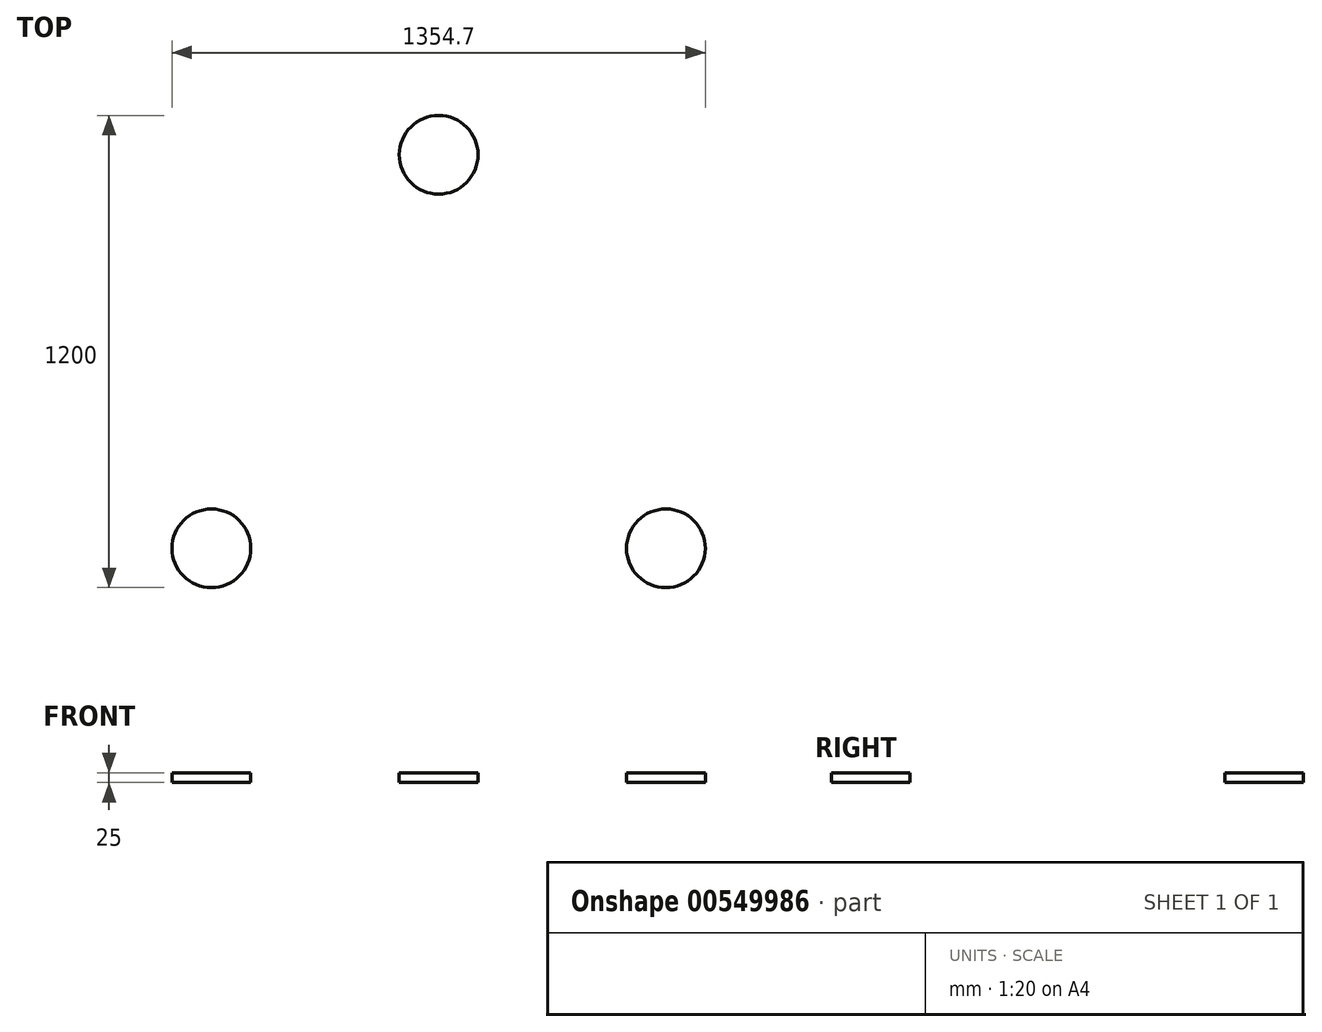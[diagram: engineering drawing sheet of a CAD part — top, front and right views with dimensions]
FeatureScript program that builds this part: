
annotation { "Feature Type Name" : "Feature", "Feature Type Description" : "" }
export const myFeature = defineFeature(function(context is Context, id is Id, definition is map)
    precondition{}
    {
        {
            var Q0;
            Q0=qCreatedBy(makeId("Top.planeOp"),FACE);
            var sketch = newSketch(context, id + "F0", { "sketchPlane" : qUnion([Q0])});
            skCircle(sketch, "E0.cCircle", {"center": v(0, 0) * mm, "radius": 333.33 * mm, "construction": true});
            skLineSegment(sketch, "E0.0", {"start": v(-577.35, -333.33) * mm, "end": v(0, 666.67) * mm, "construction": true});
            skLineSegment(sketch, "E0.1", {"start": v(0, 666.67) * mm, "end": v(577.35, -333.33) * mm, "construction": true});
            skLineSegment(sketch, "E0.2", {"start": v(577.35, -333.33) * mm, "end": v(-577.35, -333.33) * mm, "construction": true});
            skPoint(sketch, "E0.0.midPoint", {"position": v(-288.68, 166.67) * mm});
            skSolve(sketch);
        }
        {
            var Q0;
            Q0=qCreatedBy(makeId("Top.planeOp"),FACE);
            var sketch = newSketch(context, id + "F1", { "sketchPlane" : qUnion([Q0])});
            skCircle(sketch, "E1", {"center": v(0, 666.67) * mm, "radius": 100 * mm});
            skCircle(sketch, "E2", {"center": v(-577.35, -333.33) * mm, "radius": 100 * mm});
            skCircle(sketch, "E3", {"center": v(577.35, -333.33) * mm, "radius": 100 * mm});
            skSolve(sketch);
        }
        {
            var Q0;
            Q0=makeQuery(id+"F1.imprint","IMPRINT",FACE,{"disambiguationData":[TD([[makeQuery(id+"F1.imprint","IMPRINT",EDGE,{"derivedFrom":sQuery(id+"F1.wireOp",EDGE,"E1")}),1.0]])]});
            var Q1;
            Q1=makeQuery(id+"F1.imprint","IMPRINT",FACE,{"disambiguationData":[TD([[makeQuery(id+"F1.imprint","IMPRINT",EDGE,{"derivedFrom":sQuery(id+"F1.wireOp",EDGE,"E2")}),1.0]])]});
            var Q2;
            Q2=makeQuery(id+"F1.imprint","IMPRINT",FACE,{"disambiguationData":[TD([[makeQuery(id+"F1.imprint","IMPRINT",EDGE,{"derivedFrom":sQuery(id+"F1.wireOp",EDGE,"E3")}),1.0]])]});
            extrude(context, id + "F2", {"entities" : qUnion([Q0, Q1, Q2]), "oppositeDirection" : true, "depth" : 25 * mm, "offsetDistance" : 25 * mm});
        }
    });
